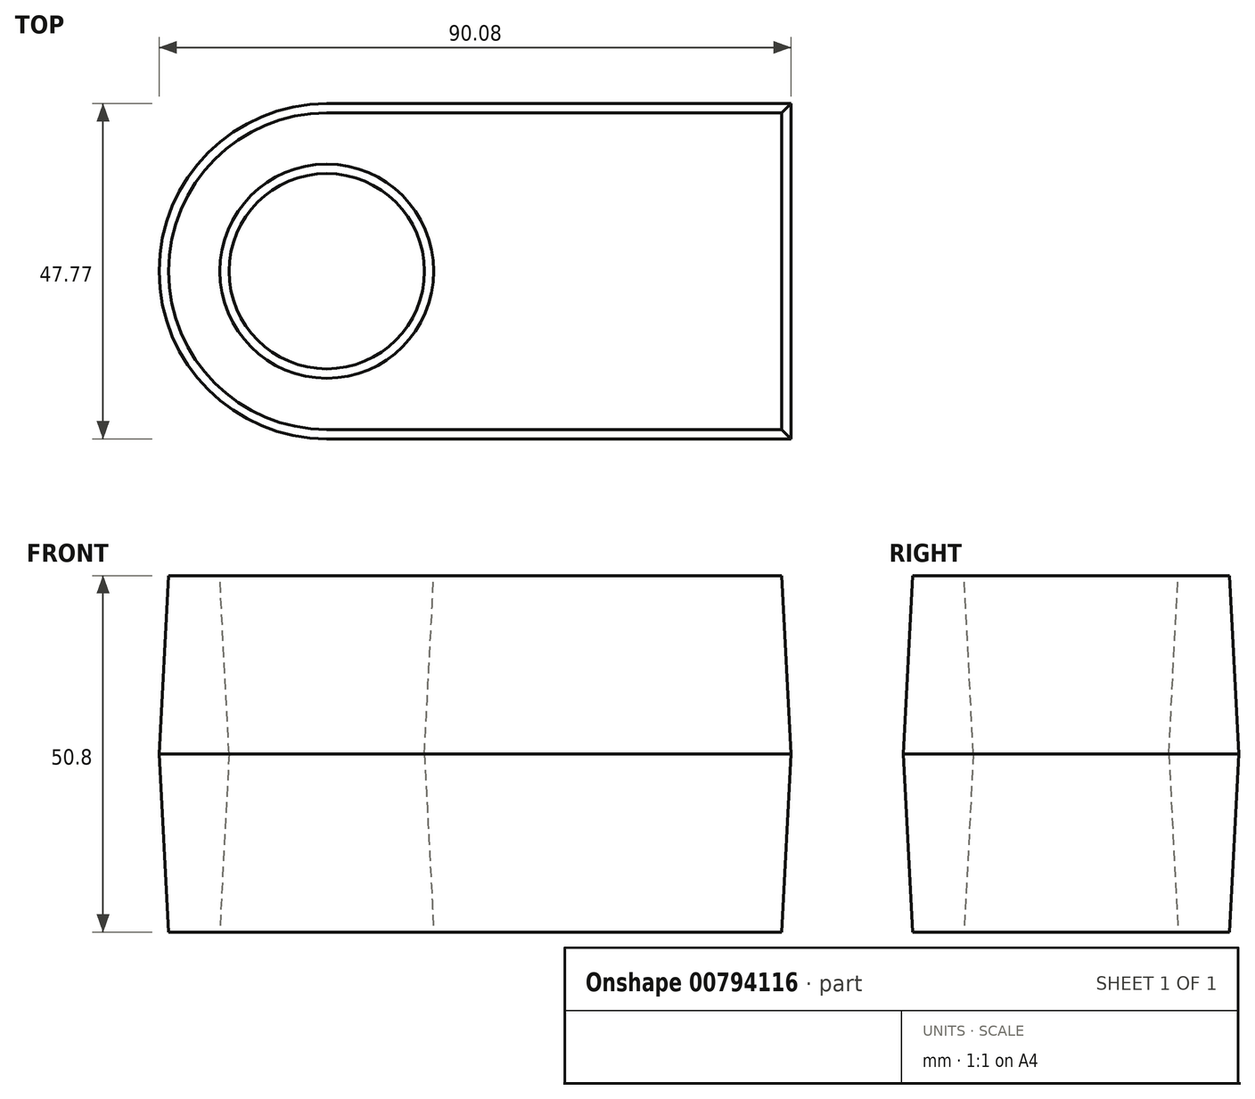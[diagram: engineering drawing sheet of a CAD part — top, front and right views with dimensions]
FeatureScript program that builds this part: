
annotation { "Feature Type Name" : "Feature", "Feature Type Description" : "" }
export const myFeature = defineFeature(function(context is Context, id is Id, definition is map)
    precondition{}
    {
        {
            var Q0;
            Q0=qCreatedBy(makeId("Top.planeOp"),FACE);
            var sketch = newSketch(context, id + "F0", { "sketchPlane" : qUnion([Q0])});
            skLineSegment(sketch, "E0.bottom", {"start": v(27.77, 23.74) * mm, "end": v(-38.42, 23.74) * mm});
            skLineSegment(sketch, "E0.top", {"start": v(27.77, -24.03) * mm, "end": v(-38.42, -24.03) * mm});
            skLineSegment(sketch, "E0.left", {"start": v(27.77, 23.74) * mm, "end": v(27.77, -24.03) * mm});
            skLineSegment(sketch, "E0.right", {"start": v(-38.42, 23.74) * mm, "end": v(-38.42, -24.03) * mm});
            skCircle(sketch, "E1", {"center": v(-38.42, -0.14) * mm, "radius": 23.89 * mm});
            skCircle(sketch, "E2", {"center": v(-38.42, -0.14) * mm, "radius": 13.92 * mm});
            skSolve(sketch);
        }
        {
            var Q0;
            Q0 = qSketchRegion(id + "F0", true);
            extrude(context, id + "F1", {"entities" : qUnion([Q0]), "depth" : 25.4 * mm, "offsetDistance" : 25.4 * mm, "hasDraft" : true, "draftAngle" : 3 * degree, "draftPullDirection" : true, "hasSecondDirection" : true, "secondDirectionOppositeDirection" : true, "secondDirectionDepth" : 25.4 * mm, "hasSecondDirectionDraft" : true, "secondDirectionDraftAngle" : 3 * degree, "secondDirectionDraftPullDirection" : true});
        }
    });
